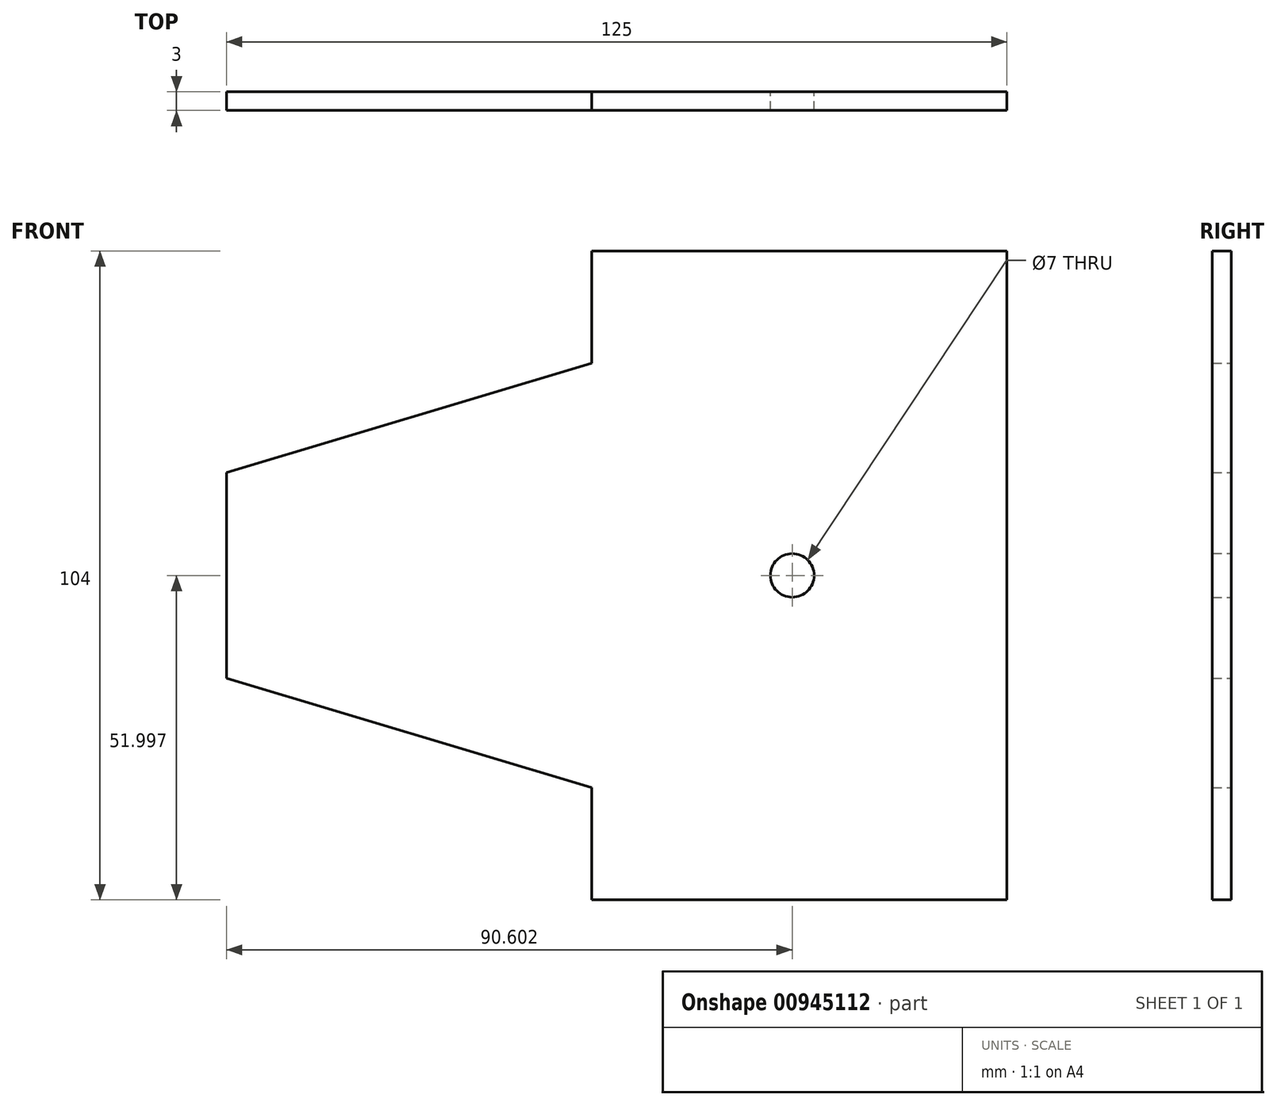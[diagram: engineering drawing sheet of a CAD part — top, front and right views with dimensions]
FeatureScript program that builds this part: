
annotation { "Feature Type Name" : "Feature", "Feature Type Description" : "" }
export const myFeature = defineFeature(function(context is Context, id is Id, definition is map)
    precondition{}
    {
        {
            var Q0;
            Q0=qCreatedBy(makeId("Front.planeOp"),FACE);
            var sketch = newSketch(context, id + "F0", { "sketchPlane" : qUnion([Q0])});
            skLineSegment(sketch, "E0.bottom", {"start": v(3.13, 97.66) * mm, "end": v(69.63, 97.66) * mm});
            skLineSegment(sketch, "E0.top", {"start": v(3.13, -6.34) * mm, "end": v(69.63, -6.34) * mm});
            skLineSegment(sketch, "E0.left", {"start": v(3.13, 97.66) * mm, "end": v(3.13, -6.34) * mm});
            skLineSegment(sketch, "E0.right", {"start": v(69.63, 97.66) * mm, "end": v(69.63, -6.34) * mm});
            skLineSegment(sketch, "E1", {"start": v(69.63, 97.66) * mm, "end": v(69.63, 45.66) * mm});
            skLineSegment(sketch, "E2", {"start": v(69.63, 45.66) * mm, "end": v(35.23, 45.66) * mm});
            skLineSegment(sketch, "E3", {"start": v(69.63, 45.66) * mm, "end": v(-55.37, 45.66) * mm});
            skLineSegment(sketch, "E4", {"start": v(-55.37, 45.66) * mm, "end": v(-55.37, 29.16) * mm});
            skLineSegment(sketch, "E5", {"start": v(-55.37, 45.66) * mm, "end": v(-55.37, 62.16) * mm});
            skLineSegment(sketch, "E6", {"start": v(3.13, 45.66) * mm, "end": v(3.13, 11.66) * mm});
            skLineSegment(sketch, "E7", {"start": v(3.13, 11.66) * mm, "end": v(3.13, 79.66) * mm});
            skLineSegment(sketch, "E8", {"start": v(3.13, 79.66) * mm, "end": v(3.13, 45.66) * mm});
            skLineSegment(sketch, "E9", {"start": v(3.13, 79.66) * mm, "end": v(-55.37, 62.16) * mm});
            skLineSegment(sketch, "E10", {"start": v(3.13, 11.66) * mm, "end": v(-55.37, 29.16) * mm});
            skSolve(sketch);
        }
        {
            var Q0;
            {var subQ0=sQuery(id+"F0.wireOp",EDGE,"E5");Q0=makeQuery(id+"F0.imprint","IMPRINT",FACE,{"disambiguationData":[TD([[makeQuery(id+"F0.imprint","IMPRINT",EDGE,{"derivedFrom":subQ0}),-1.0]])]});}
            var Q1;
            {var subQ4=sQuery(id+"F0.wireOp",EDGE,"E0.bottom");Q1=makeQuery(id+"F0.imprint","IMPRINT",FACE,{"disambiguationData":[TD([[makeQuery(id+"F0.imprint","IMPRINT",EDGE,{"derivedFrom":subQ4}),-1.0]])]});}
            var Q2;
            {var subQ2=sQuery(id+"F0.wireOp",EDGE,"E0.top");Q2=makeQuery(id+"F0.imprint","IMPRINT",FACE,{"disambiguationData":[TD([[makeQuery(id+"F0.imprint","IMPRINT",EDGE,{"derivedFrom":subQ2}),1.0]])]});}
            var Q3;
            {var subQ0=sQuery(id+"F0.wireOp",EDGE,"E4");Q3=makeQuery(id+"F0.imprint","IMPRINT",FACE,{"disambiguationData":[TD([[makeQuery(id+"F0.imprint","IMPRINT",EDGE,{"derivedFrom":subQ0}),1.0]])]});}
            extrude(context, id + "F1", {"entities" : qUnion([Q0, Q1, Q2, Q3]), "depth" : 3 * mm, "offsetDistance" : 25 * mm});
        }
        {
            var Q0;
            Q0=sQuery(id+"F0.wireOp",VERTEX,"E2.end");
            var Q1;
            Q1=makeQuery(id+"F1.opExtrude","SWEPT_BODY",BODY,{"disambiguationData":[OSD([sQuery(id+"F0.wireOp",EDGE,"E0.bottom"),sQuery(id+"F0.wireOp",EDGE,"E0.top"),sQuery(id+"F0.wireOp",EDGE,"E0.left"),sQuery(id+"F0.wireOp",EDGE,"E0.right"),sQuery(id+"F0.wireOp",EDGE,"E1"),sQuery(id+"F0.wireOp",EDGE,"E4"),sQuery(id+"F0.wireOp",EDGE,"E5"),sQuery(id+"F0.wireOp",EDGE,"E9"),sQuery(id+"F0.wireOp",EDGE,"E10")])]});
            hole(context, id + "F2", {"style" : HoleStyle.SIMPLE, "endStyle" : HoleEndStyle.BLIND, "oppositeDirection" : true, "holeDiameter" : 7 * mm, "majorDiameter" : 5 * mm, "holeDepth" : 10 * mm, "isTappedThrough" : true, "tappedDepth" : 12 * mm, "tapClearance" : 3, "locations" : qUnion([Q0]), "scope" : qUnion([Q1])});
        }
    });
